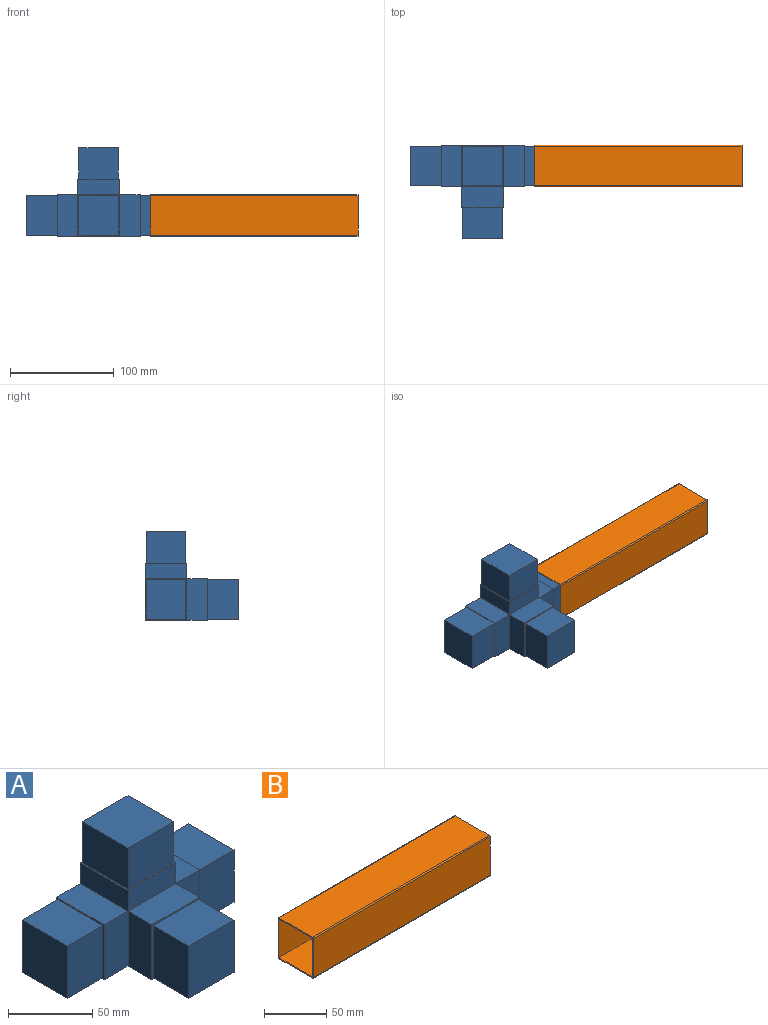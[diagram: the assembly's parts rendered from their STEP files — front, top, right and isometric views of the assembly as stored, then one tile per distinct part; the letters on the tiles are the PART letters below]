
ASSEMBLY  parts=2 mates=1
PART A: 36 faces, bbox 140x90x85 mm
  f0: plane 40x40mm, normal (0,0,1), area 156mm2, adj f8,f13,f14,f15,f31,f32,f33,f34
  f1: plane 40x20mm, normal (0,0,1), area 800mm2, adj f8,f9,f10,f15
  f2: plane 40x20mm, normal (0,0,1), area 800mm2, adj f3,f4,f5,f13
  f3: plane 40x20mm, normal (-1,0,0), area 800mm2, adj f2,f4,f10,f12
  f4: plane 40x40mm, normal (0,-1,0), area 156mm2, adj f2,f3,f5,f12,f26,f27,f28,f29
  f5: plane 40x20mm, normal (1,0,0), area 800mm2, adj f2,f4,f6,f12
  f6: plane 40x20mm, normal (0,-1,0), area 800mm2, adj f5,f7,f11,f12
  f7: plane 40x40mm, normal (1,0,0), area 156mm2, adj f6,f8,f11,f12,f21,f22,f23,f24
  f8: plane 80x55mm, normal (0,1,0), area 3800mm2, adj f0,f1,f7,f9,f11,f12,f14,f15
  f9: plane 40x40mm, normal (-1,0,0), area 156mm2, adj f1,f8,f10,f12,f16,f17,f18,f19
  f10: plane 40x20mm, normal (0,-1,0), area 800mm2, adj f1,f3,f9,f12
  f11: plane 40x20mm, normal (0,0,1), area 800mm2, adj f6,f7,f8,f14
  f12: plane 80x60mm, normal (0,0,-1), area 4000mm2, adj f3,f4,f5,f6,f7,f8,f9,f10
  f13: plane 40x15mm, normal (0,-1,0), area 600mm2, adj f0,f2,f14,f15
  f14: plane 40x15mm, normal (1,0,0), area 600mm2, adj f0,f8,f11,f13
  f15: plane 40x15mm, normal (-1,0,0), area 600mm2, adj f0,f1,f8,f13
  f16: plane 38x30mm, normal (0,-1,0), area 1140mm2, adj f9,f17,f19,f20
  f17: plane 38x30mm, normal (0,0,1), area 1140mm2, adj f9,f16,f18,f20
  f18: plane 38x30mm, normal (0,1,0), area 1140mm2, adj f9,f17,f19,f20
  f19: plane 38x30mm, normal (0,0,-1), area 1140mm2, adj f9,f16,f18,f20
  f20: plane 38x38mm, normal (-1,0,0), area 1444mm2, adj f16,f17,f18,f19
  f21: plane 38x30mm, normal (0,-1,0), area 1140mm2, adj f7,f22,f24,f25
  f22: plane 38x30mm, normal (0,0,1), area 1140mm2, adj f7,f21,f23,f25
  f23: plane 38x30mm, normal (0,1,0), area 1140mm2, adj f7,f22,f24,f25
  f24: plane 38x30mm, normal (0,0,-1), area 1140mm2, adj f7,f21,f23,f25
  f25: plane 38x38mm, normal (1,0,0), area 1444mm2, adj f21,f22,f23,f24
  f26: plane 38x30mm, normal (1,0,0), area 1140mm2, adj f4,f27,f29,f30
  f27: plane 38x30mm, normal (0,0,1), area 1140mm2, adj f4,f26,f28,f30
  f28: plane 38x30mm, normal (-1,0,0), area 1140mm2, adj f4,f27,f29,f30
  f29: plane 38x30mm, normal (0,0,-1), area 1140mm2, adj f4,f26,f28,f30
  f30: plane 38x38mm, normal (0,-1,0), area 1444mm2, adj f26,f27,f28,f29
  f31: plane 38x30mm, normal (0,-1,0), area 1140mm2, adj f0,f32,f34,f35
  f32: plane 38x30mm, normal (1,0,0), area 1140mm2, adj f0,f31,f33,f35
  f33: plane 38x30mm, normal (0,1,0), area 1140mm2, adj f0,f32,f34,f35
  f34: plane 38x30mm, normal (-1,0,0), area 1140mm2, adj f0,f31,f33,f35
  f35: plane 38x38mm, normal (0,0,1), area 1444mm2, adj f31,f32,f33,f34
PART B: 14 faces, bbox 200x40x40 mm
  f0: plane 200x38mm, normal (0,1,0), area 7600mm2, adj f1,f7,f8,f9
  f1: cylinder r=1mm len=200mm, axis (-1,0,0), area 314.2mm2, adj f0,f2,f8,f9
  f2: plane 200x38mm, normal (0,0,1), area 7600mm2, adj f1,f3,f8,f9
  f3: cylinder r=1mm len=200mm, axis (-1,0,0), area 314.2mm2, adj f2,f4,f8,f9
  f4: plane 200x38mm, normal (0,-1,0), area 7600mm2, adj f3,f5,f8,f9
  f5: cylinder r=1mm len=200mm, axis (-1,0,0), area 314.2mm2, adj f4,f6,f8,f9
  f6: plane 200x38mm, normal (0,0,-1), area 7600mm2, adj f5,f7,f8,f9
  f7: cylinder r=1mm len=200mm, axis (-1,0,0), area 314.2mm2, adj f0,f6,f8,f9
  f8: plane 40x40mm, normal (1,0,0), area 155.1mm2, adj f0,f1,f2,f3,f4,f5,f6,f7
  f9: plane 40x40mm, normal (-1,0,0), area 155.1mm2, adj f0,f1,f2,f3,f4,f5,f6,f7
  f10: plane 200x38mm, normal (0,-1,0), area 7600mm2, adj f8,f9,f11,f13
  f11: plane 200x38mm, normal (0,0,-1), area 7600mm2, adj f8,f9,f10,f12
  f12: plane 200x38mm, normal (0,1,0), area 7600mm2, adj f8,f9,f11,f13
  f13: plane 200x38mm, normal (0,0,1), area 7600mm2, adj f8,f9,f10,f12
PLACE A t=(-38.15,-15.93,9.15)mm fixed
PLACE B t=(111.85,-15.93,9.15)mm
MATE fastened A.f7 <-> B.f3  axis (1,0,0) through (1.85,-34.93,28.15)mm
